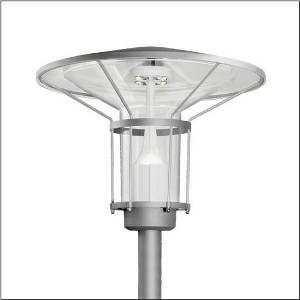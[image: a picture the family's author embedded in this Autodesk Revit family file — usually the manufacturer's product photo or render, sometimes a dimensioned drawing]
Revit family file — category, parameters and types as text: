
# Revit family: laterne_classic_iq___pl1_2s_5xa5245rf14h_f81d
name_source: partatom
category: Lighting Fixtures
units: mm (PartAtom-declared; Revit-internal decimal feet)

## family parameters
Cut with Voids When Loaded = No
Host = Face
Light Source = No
Part Type = Normal
Room Calculation Point = No
Round Connector Dimension = Use Diameter
Shared = No

## types (1)
- --- (1 x LED, 2670 lm, 18.5 W, 4000K)
    Apparent Load = 19 VA
    CIE Flux Codes = 21 60 93 97 100
    Color Rendering = 70
    Color Temperature = 4000K
    Default Elevation = 1800 mm
    Description = Lantern Classic iQ, mast luminaire, Module 540 iQ-SR, primary light control with 3 zone facetted reflector, of plastic, silver coated, highly specular, structured, primary optical cover: cover, of PMMA, transparent, light distribution: PL1.2s, light emission: direct distribution, primary light characteristic: symmetric, installation type: post-top, LED, High Power LED, rated luminous flux: 2.670lm, luminous efficacy: 144lm/W, light colour: 740, colour temperature: 4000K, control gear: iQ Street-Remote, control: pre-setting: logarithmic dimming characteristic, Street-Remote, Auto-Match, Temp-Guard, Lumen-Switch, Night-Set, Smart-Wire, Light-Fading, Desk-Remote (wireless, voltage-free reading and setting of iQ features in the workshop via application-optimized NFC function/RFID function), optimised constant luminous flux control (CLO 2.0), with terminal, 6-pole, max. 2.5mm², mains connection: 230..240V, AC, 50/60Hz, start of lifetime: 19W, end of service life: 20W, reduction: 9W, luminaire housing, upper part, of glass-fibre reinforced polyester, coated, Siteco® metallic grey (DB 702S), diameter: 750mm, height: 596mm, spigot size: d x l = 76 x 70mm (post-top) | with reducer (optional accessory) 60 x 70mm, mounting height: 3..5m, post-top mast mounting element, of diecast aluminium, coated, Siteco® metallic grey (DB 702S), Module 540 iQ-SR, traffic white (RAL 9016), equipment: standard, protection rating (complete): IP65, insulation class (complete): insulation class II (safety insulation), certification: CE, ENEC, VDE, packaging unit: 1 piece

Light Distribution: PL1.2s
    Height = 596 mm
    Lamp = 1 x LED
    Lamp Light Flux = 2670 lm
    Lamp Power = 18.5 W
    Lamp count = 1
    Length = 750 mm
    Luminous efficacy = 144 lm/W
    Manufacturer = Siteco
    ModVariant = No
    Model = 5XA5245RF14H
    Number of Poles = 1
    OnlyDefault = Yes
    Power Factor = 1
    Product Name = Laterne Classic iQ | PL1.2s
    Product group = mast luminaire | pylon top
    ProductGroupID = 6100
    Protection Class = Protection class II
    Protection Degree = IP 65
    RLX_Detail_Level = 1
    RLX_Emergency_Light_Flux = 0 lm
    RLX_Emergency_Type = 0
    RLX_Emergency_Type_DB = No
    RlxData = <blob elided: 37853 chars, md5=97163721>
    Socket = socket
    Standby Power = 0 W
    System Light Flux = 2670 lm
    System Power = 19 W
    Type Comments = factory setting: luminous flux: 100 % | dim-lin: 254 | 385 mA
    Type Image = l_1006052.jpg
    URL = http://relux.com
    VarID = @adj_167183
    Voltage = 0 V
    Weight = 0.00 kg
    Width = 0 mm  [stored 0 ft]

note: [stored X ft] marks values corroborated as IEEE doubles in the binary element streams (Revit-internal decimal feet)

## geometry (parser evidence)
native form markers: Blend x4, Sweep x9
no freeform markers — native parametric forms only
